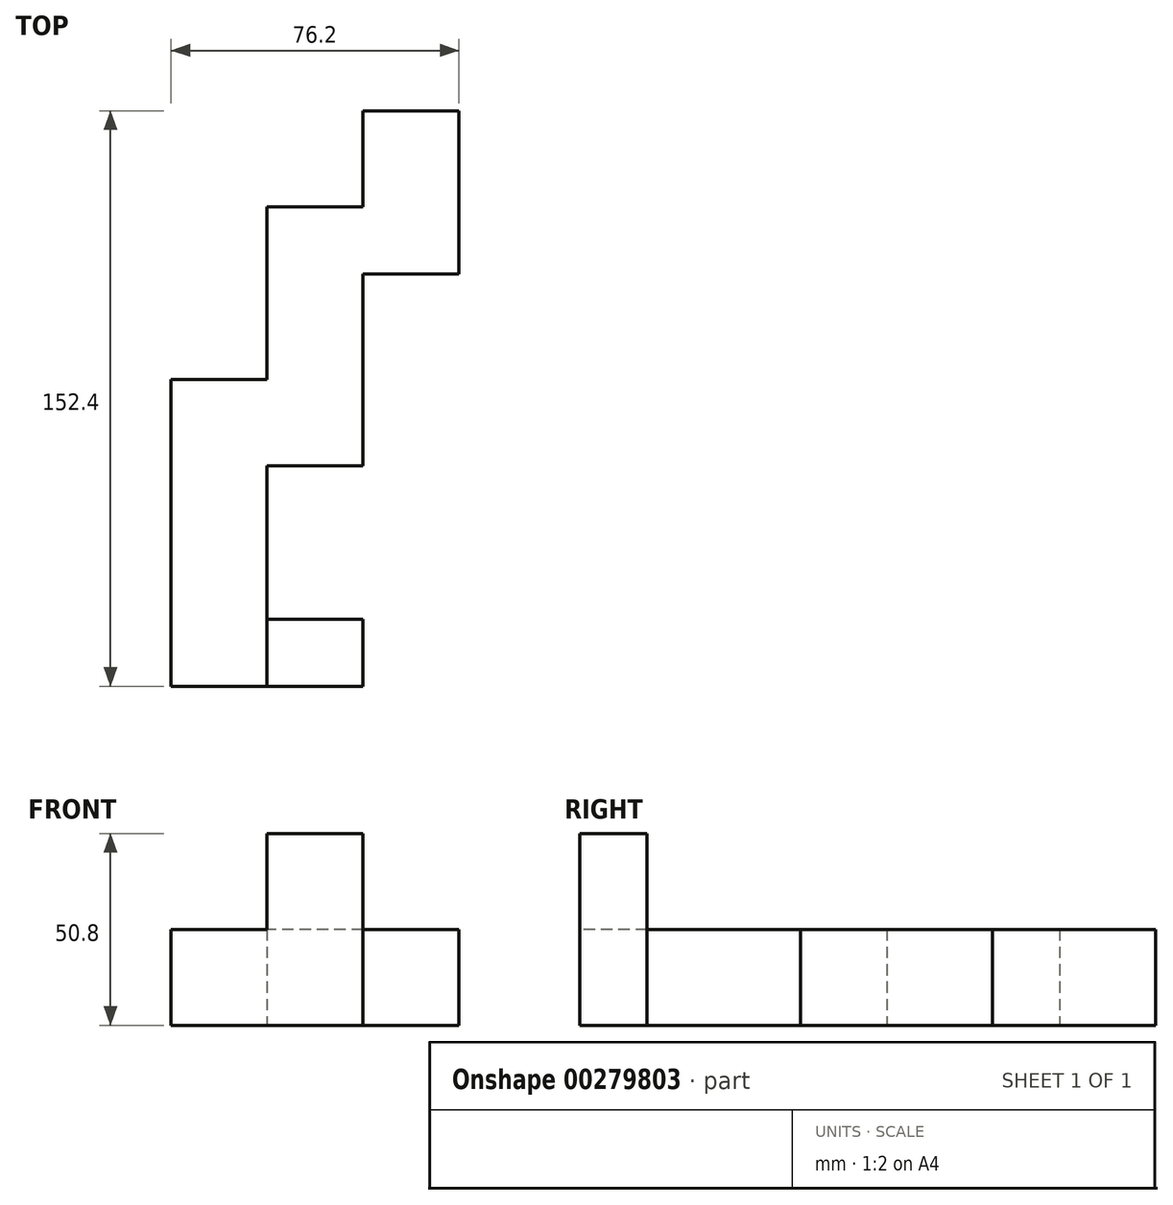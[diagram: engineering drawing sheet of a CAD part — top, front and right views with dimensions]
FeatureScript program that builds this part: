
annotation { "Feature Type Name" : "Feature", "Feature Type Description" : "" }
export const myFeature = defineFeature(function(context is Context, id is Id, definition is map)
    precondition{}
    {
        {
            var Q0;
            Q0=qCreatedBy(makeId("Right.planeOp"),FACE);
            var sketch = newSketch(context, id + "F0", { "sketchPlane" : qUnion([Q0])});
            skLineSegment(sketch, "E0.bottom", {"start": v(57.98, -24.02) * mm, "end": v(14.8, -24.02) * mm});
            skLineSegment(sketch, "E0.top", {"start": v(57.98, -49.42) * mm, "end": v(14.8, -49.42) * mm});
            skLineSegment(sketch, "E0.left", {"start": v(57.98, -24.02) * mm, "end": v(57.98, -49.42) * mm});
            skLineSegment(sketch, "E0.right", {"start": v(14.8, -24.02) * mm, "end": v(14.8, -49.42) * mm});
            skSolve(sketch);
        }
        {
            var Q0;
            Q0=makeQuery(id+"F0.imprint","IMPRINT",FACE,{"disambiguationData":[TD([[makeQuery(id+"F0.imprint","IMPRINT",EDGE,{"derivedFrom":sQuery(id+"F0.wireOp",EDGE,"E0.bottom")}),1.0]])]});
            extrude(context, id + "F1", {"entities" : qUnion([Q0]), "depth" : 25.4 * mm});
        }
        {
            var Q0;
            Q0=makeQuery(id+"F1.opExtrude","CAP_FACE",FACE,{"disambiguationData":[OSD([sQuery(id+"F0.wireOp",EDGE,"E0.bottom"),sQuery(id+"F0.wireOp",EDGE,"E0.top"),sQuery(id+"F0.wireOp",EDGE,"E0.left"),sQuery(id+"F0.wireOp",EDGE,"E0.right")])],"isStart":true});
            var sketch = newSketch(context, id + "F2", { "sketchPlane" : qUnion([Q0])});
            skLineSegment(sketch, "E1", {"start": v(-32.58, -24.02) * mm, "end": v(-32.58, -49.42) * mm});
            skSolve(sketch);
        }
        {
            var Q0;
            {var subQ0=sQuery(id+"F2.wireOp",EDGE,"E1");Q0=makeQuery(id+"F2.imprint","IMPRINT",FACE,{"disambiguationData":[TD([[makeQuery(id+"F2.imprint","IMPRINT",EDGE,{"derivedFrom":subQ0}),1.0]])]});}
            extrude(context, id + "F3", {"entities" : qUnion([Q0]), "operationType" : NewBodyOperationType.ADD, "depth" : 25.4 * mm});
        }
        {
            var Q0;
            {var subQ0=sQuery(id+"F0.wireOp",EDGE,"E0.right");Q0=makeQuery(id+"F3.boolean.opBoolean","MERGE",FACE,{"derivedFrom":[makeQuery(id+"F1.opExtrude","SWEPT_FACE",FACE,{"disambiguationData":[OSD([subQ0])]}),makeQuery(id+"F3.opExtrude","SWEPT_FACE",FACE,{"disambiguationData":[OSD([subQ0])]})]});}
            var sketch = newSketch(context, id + "F4", { "sketchPlane" : qUnion([Q0])});
            skLineSegment(sketch, "E2", {"start": v(0, -24.02) * mm, "end": v(0, -49.42) * mm});
            skSolve(sketch);
        }
        {
            var Q0;
            Q0 = qSketchRegion(id + "F4", true);
            var Q1;
            {var subQ0=sQuery(id+"F4.wireOp",EDGE,"E2");Q1=makeQuery(id+"F4.imprint","IMPRINT",FACE,{"disambiguationData":[TD([[makeQuery(id+"F4.imprint","IMPRINT",EDGE,{"derivedFrom":subQ0}),-1.0]])]});}
            extrude(context, id + "F5", {"entities" : qUnion([Q0, Q1]), "operationType" : NewBodyOperationType.ADD, "depth" : 50.8 * mm});
        }
        {
            var Q0;
            {var subQ0=sQuery(id+"F0.wireOp",EDGE,"E0.right");Q0=makeQuery(id+"F5.boolean.opBoolean","MERGE",FACE,{"derivedFrom":[makeQuery(id+"F3.opExtrude","CAP_FACE",FACE,{"disambiguationData":[OSD([sQuery(id+"F0.wireOp",EDGE,"E0.bottom"),sQuery(id+"F0.wireOp",EDGE,"E0.top"),subQ0,sQuery(id+"F2.wireOp",EDGE,"E1")])],"isStart":false}),makeQuery(id+"F5.opExtrude","SWEPT_FACE",FACE,{"disambiguationData":[OSD([subQ0])]})]});}
            var sketch = newSketch(context, id + "F6", { "sketchPlane" : qUnion([Q0])});
            skLineSegment(sketch, "E3", {"start": v(-9.72, -24.02) * mm, "end": v(-9.72, -49.42) * mm});
            skLineSegment(sketch, "E4", {"start": v(13.14, -24.02) * mm, "end": v(13.14, -49.42) * mm});
            skSolve(sketch);
        }
        {
            var Q0;
            {var subQ0=sQuery(id+"F6.wireOp",EDGE,"E4");Q0=makeQuery(id+"F6.imprint","IMPRINT",FACE,{"disambiguationData":[TD([[makeQuery(id+"F6.imprint","IMPRINT",EDGE,{"derivedFrom":subQ0}),1.0]])]});}
            extrude(context, id + "F7", {"entities" : qUnion([Q0]), "operationType" : NewBodyOperationType.ADD, "depth" : 25.4 * mm});
        }
        {
            var Q0;
            {var subQ0=sQuery(id+"F0.wireOp",EDGE,"E0.right");Q0=makeQuery(id+"F7.boolean.opBoolean","MERGE",FACE,{"derivedFrom":[makeQuery(id+"F5.opExtrude","CAP_FACE",FACE,{"disambiguationData":[OSD([sQuery(id+"F0.wireOp",EDGE,"E0.bottom"),sQuery(id+"F0.wireOp",EDGE,"E0.top"),subQ0,sQuery(id+"F4.wireOp",EDGE,"E2")])],"isStart":false}),makeQuery(id+"F7.opExtrude","SWEPT_FACE",FACE,{"disambiguationData":[OSD([subQ0])]})]});}
            var sketch = newSketch(context, id + "F8", { "sketchPlane" : qUnion([Q0])});
            skLineSegment(sketch, "E5", {"start": v(-25.4, -24.02) * mm, "end": v(-25.4, -49.42) * mm});
            skSolve(sketch);
        }
        {
            var Q0;
            {var subQ0=sQuery(id+"F8.wireOp",EDGE,"E5");Q0=makeQuery(id+"F8.imprint","IMPRINT",FACE,{"disambiguationData":[TD([[makeQuery(id+"F8.imprint","IMPRINT",EDGE,{"derivedFrom":subQ0}),-1.0]])]});}
            extrude(context, id + "F9", {"entities" : qUnion([Q0]), "operationType" : NewBodyOperationType.ADD, "depth" : 58.42 * mm});
        }
        {
            var Q0;
            Q0=makeQuery(id+"F9.opExtrude","SWEPT_FACE",FACE,{"disambiguationData":[OSD([sQuery(id+"F8.wireOp",EDGE,"E5")])]});
            var sketch = newSketch(context, id + "F10", { "sketchPlane" : qUnion([Q0])});
            skLineSegment(sketch, "E6", {"start": v(-76.64, -24.02) * mm, "end": v(-76.64, -49.42) * mm});
            skSolve(sketch);
        }
        {
            var Q0;
            Q0 = qSketchRegion(id + "F10", true);
            var Q1;
            {var subQ0=sQuery(id+"F10.wireOp",EDGE,"E6");Q1=makeQuery(id+"F10.imprint","IMPRINT",FACE,{"disambiguationData":[TD([[makeQuery(id+"F10.imprint","IMPRINT",EDGE,{"derivedFrom":subQ0}),-1.0]])]});}
            extrude(context, id + "F11", {"entities" : qUnion([Q0, Q1]), "operationType" : NewBodyOperationType.ADD, "depth" : 25.4 * mm});
        }
        {
            var Q0;
            {var subQ0=sQuery(id+"F0.wireOp",EDGE,"E0.right");var subQ1=sQuery(id+"F0.wireOp",EDGE,"E0.bottom");Q0=makeQuery(id+"F11.boolean.opBoolean","MERGE",FACE,{"derivedFrom":[makeQuery(id+"F9.boolean.opBoolean","MERGE",FACE,{"derivedFrom":[makeQuery(id+"F7.boolean.opBoolean","MERGE",FACE,{"derivedFrom":[makeQuery(id+"F5.boolean.opBoolean","MERGE",FACE,{"derivedFrom":[makeQuery(id+"F3.boolean.opBoolean","MERGE",FACE,{"derivedFrom":[makeQuery(id+"F1.opExtrude","SWEPT_FACE",FACE,{"disambiguationData":[OSD([subQ1])]}),makeQuery(id+"F3.opExtrude","SWEPT_FACE",FACE,{"disambiguationData":[OSD([subQ1])]})]}),makeQuery(id+"F5.opExtrude","SWEPT_FACE",FACE,{"disambiguationData":[OSD([subQ1,subQ0])]})]}),makeQuery(id+"F7.opExtrude","SWEPT_FACE",FACE,{"disambiguationData":[OSD([subQ1,subQ0])]})]}),makeQuery(id+"F9.opExtrude","SWEPT_FACE",FACE,{"disambiguationData":[OSD([subQ1,subQ0])]})]}),makeQuery(id+"F11.opExtrude","SWEPT_FACE",FACE,{"disambiguationData":[OSD([subQ1,subQ0,sQuery(id+"F8.wireOp",EDGE,"E5")])]})]});}
            var sketch = newSketch(context, id + "F12", { "sketchPlane" : qUnion([Q0])});
            skLineSegment(sketch, "E7", {"start": v(-25.4, -76.64) * mm, "end": v(-25.4, -94.42) * mm});
            skSolve(sketch);
        }
        {
            var Q0;
            {var subQ0=sQuery(id+"F12.wireOp",EDGE,"E7");Q0=makeQuery(id+"F12.imprint","IMPRINT",FACE,{"disambiguationData":[TD([[makeQuery(id+"F12.imprint","IMPRINT",EDGE,{"derivedFrom":subQ0}),1.0]])]});}
            extrude(context, id + "F13", {"entities" : qUnion([Q0]), "operationType" : NewBodyOperationType.ADD, "depth" : 25.4 * mm});
        }
    });
